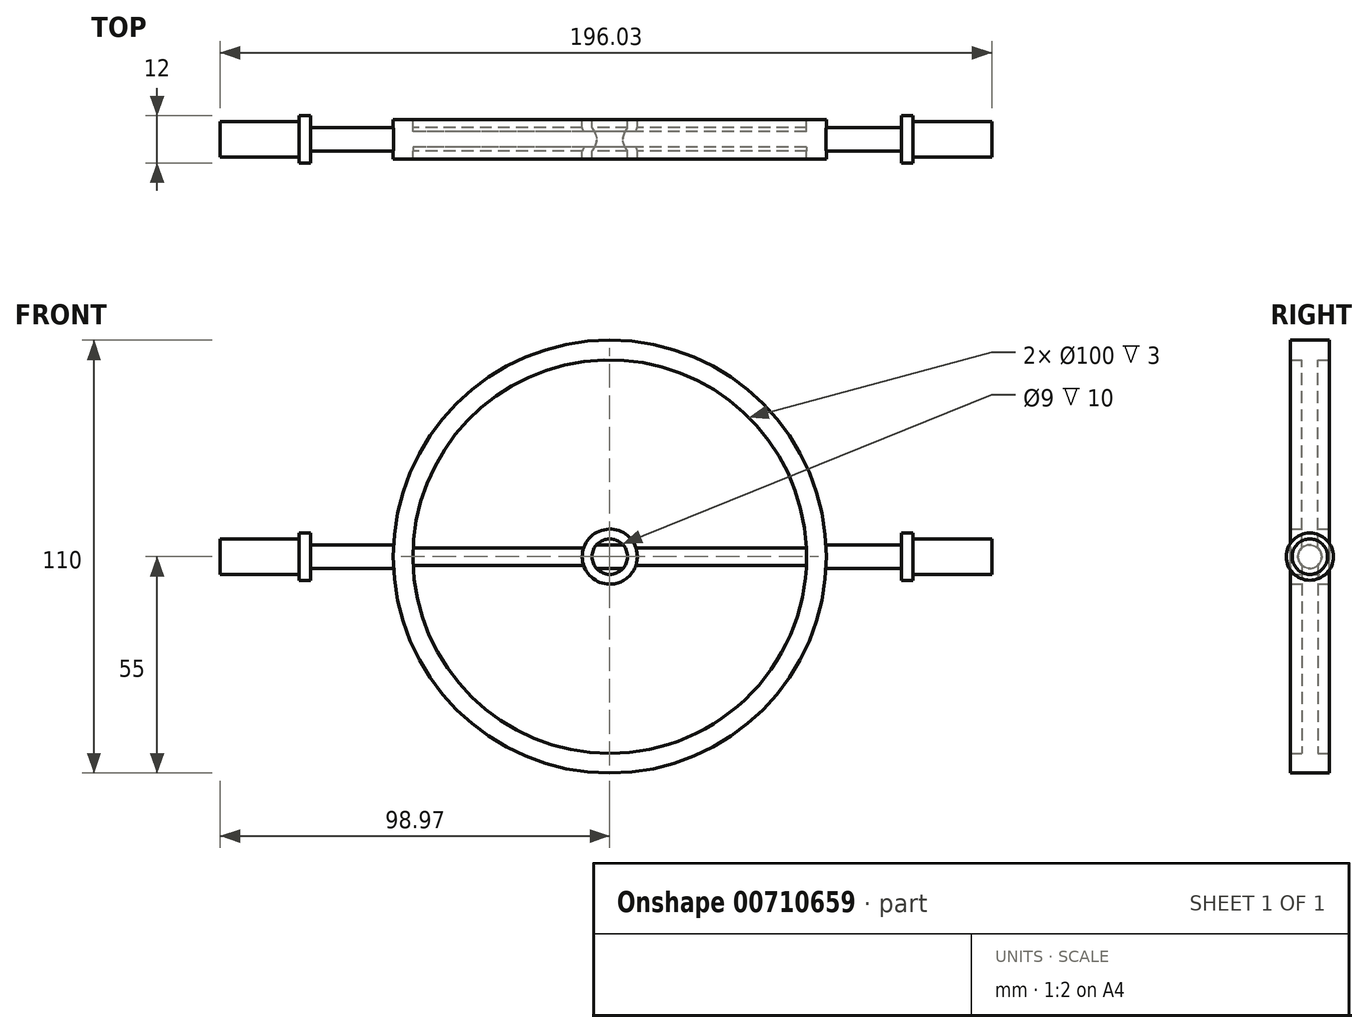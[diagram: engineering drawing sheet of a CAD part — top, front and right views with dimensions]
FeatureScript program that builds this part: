
annotation { "Feature Type Name" : "Feature", "Feature Type Description" : "" }
export const myFeature = defineFeature(function(context is Context, id is Id, definition is map)
    precondition{}
    {
        {
            var Q0;
            Q0=qCreatedBy(makeId("Front.planeOp"),FACE);
            var sketch = newSketch(context, id + "F0", { "sketchPlane" : qUnion([Q0])});
            skCircle(sketch, "E0", {"center": v(0, 0) * mm, "radius": 55 * mm});
            skCircle(sketch, "E1", {"center": v(0, 0) * mm, "radius": 4.5 * mm});
            skCircle(sketch, "E2", {"center": v(0, 0) * mm, "radius": 7 * mm});
            skCircle(sketch, "E3", {"center": v(0, 0) * mm, "radius": 50 * mm});
            skSolve(sketch);
        }
        {
            var Q0;
            Q0=makeQuery(id+"F0.imprint","IMPRINT",FACE,{"disambiguationData":[TD([[makeQuery(id+"F0.imprint","IMPRINT",EDGE,{"derivedFrom":sQuery(id+"F0.wireOp",EDGE,"E2")}),-1.0]])]});
            extrude(context, id + "F1", {"entities" : qUnion([Q0]), "endBound" : BoundingType.SYMMETRIC, "depth" : 4 * mm, "offsetDistance" : 25 * mm});
        }
        {
            var Q0;
            Q0=makeQuery(id+"F0.imprint","IMPRINT",FACE,{"disambiguationData":[TD([[makeQuery(id+"F0.imprint","IMPRINT",EDGE,{"derivedFrom":sQuery(id+"F0.wireOp",EDGE,"E0")}),1.0]])]});
            extrude(context, id + "F2", {"entities" : qUnion([Q0]), "operationType" : NewBodyOperationType.ADD, "endBound" : BoundingType.SYMMETRIC, "depth" : 10 * mm, "offsetDistance" : 25 * mm});
        }
        {
            var Q0;
            Q0=qCreatedBy(makeId("Front.planeOp"),FACE);
            var sketch = newSketch(context, id + "F3", { "sketchPlane" : qUnion([Q0])});
            skLineSegment(sketch, "E4", {"start": v(97.06, 0) * mm, "end": v(97.06, 4.5) * mm});
            skLineSegment(sketch, "E5", {"start": v(97.06, 4.5) * mm, "end": v(77.06, 4.5) * mm});
            skLineSegment(sketch, "E6", {"start": v(77.06, 4.5) * mm, "end": v(77.06, 6) * mm});
            skLineSegment(sketch, "E7", {"start": v(77.06, 6) * mm, "end": v(74.06, 6) * mm});
            skLineSegment(sketch, "E8", {"start": v(74.06, 6) * mm, "end": v(74.06, 3) * mm});
            skLineSegment(sketch, "E9", {"start": v(74.06, 3) * mm, "end": v(-75.97, 3) * mm});
            skLineSegment(sketch, "E10", {"start": v(-75.97, 3) * mm, "end": v(-75.97, 6) * mm});
            skLineSegment(sketch, "E11", {"start": v(-75.97, 6) * mm, "end": v(-78.97, 6) * mm});
            skLineSegment(sketch, "E12", {"start": v(-78.97, 6) * mm, "end": v(-78.97, 4.5) * mm});
            skLineSegment(sketch, "E13", {"start": v(-78.97, 4.5) * mm, "end": v(-98.97, 4.5) * mm});
            skLineSegment(sketch, "E14", {"start": v(-98.97, 4.5) * mm, "end": v(-98.97, 0) * mm});
            skLineSegment(sketch, "E15", {"start": v(-98.97, 0) * mm, "end": v(97.06, 0) * mm});
            skSolve(sketch);
        }
        {
            var Q0;
            Q0=makeQuery(id+"F3.imprint","IMPRINT",FACE,{"disambiguationData":[TD([[makeQuery(id+"F3.imprint","IMPRINT",EDGE,{"derivedFrom":sQuery(id+"F3.wireOp",EDGE,"E4")}),1.0]])]});
            var Q1;
            Q1=sQuery(id+"F3.wireOp",EDGE,"E15");
            revolve(context, id + "F4", {"surfaceOperationType" : NewSurfaceOperationType.NEW, "entities" : qUnion([Q0]), "axis" : qUnion([Q1]), "revolveType" : RevolveType.FULL});
        }
        {
            var Q0;
            Q0=makeQuery(id+"F0.imprint","IMPRINT",FACE,{"disambiguationData":[TD([[makeQuery(id+"F0.imprint","IMPRINT",EDGE,{"derivedFrom":sQuery(id+"F0.wireOp",EDGE,"E1")}),-1.0]])]});
            extrude(context, id + "F5", {"entities" : qUnion([Q0]), "operationType" : NewBodyOperationType.ADD, "endBound" : BoundingType.SYMMETRIC, "depth" : 10 * mm, "offsetDistance" : 25 * mm});
        }
    });
